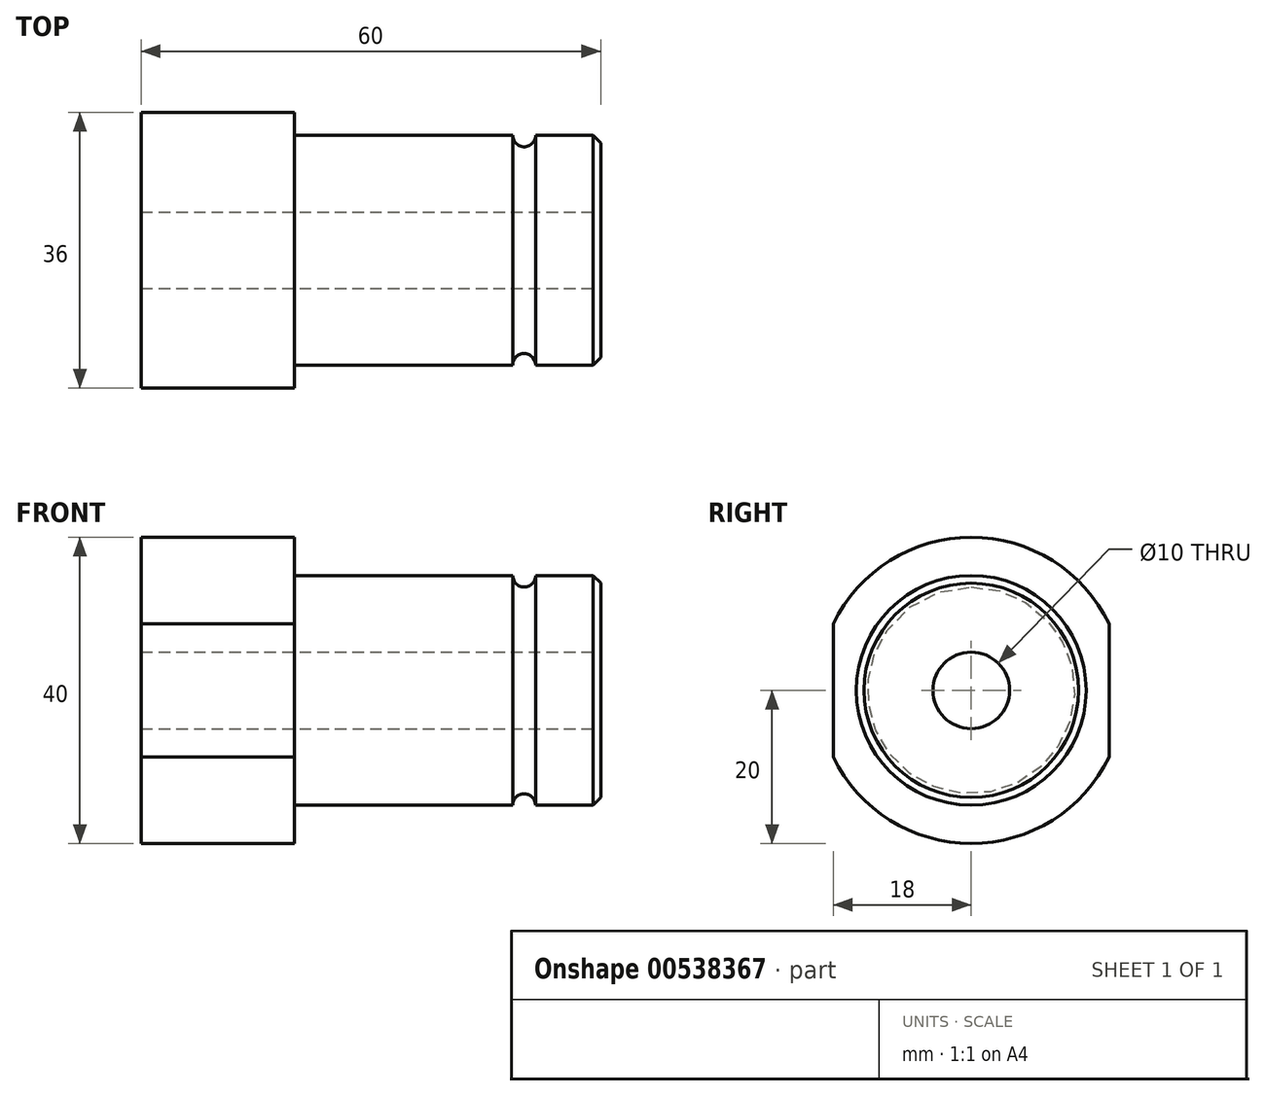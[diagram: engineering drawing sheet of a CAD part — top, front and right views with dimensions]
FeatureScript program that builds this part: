
annotation { "Feature Type Name" : "Feature", "Feature Type Description" : "" }
export const myFeature = defineFeature(function(context is Context, id is Id, definition is map)
    precondition{}
    {
        {
            var Q0;
            Q0=qCreatedBy(makeId("Front.planeOp"),FACE);
            var sketch = newSketch(context, id + "F0", { "sketchPlane" : qUnion([Q0])});
            skLineSegment(sketch, "E0", {"start": v(-37.15, 0) * mm, "end": v(-37.15, 20) * mm});
            skLineSegment(sketch, "E1", {"start": v(-37.15, 20) * mm, "end": v(-17.15, 20) * mm});
            skLineSegment(sketch, "E2", {"start": v(-17.15, 20) * mm, "end": v(-17.15, 15) * mm});
            skLineSegment(sketch, "E3", {"start": v(-17.15, 15) * mm, "end": v(22.85, 15) * mm});
            skLineSegment(sketch, "E4", {"start": v(22.85, 15) * mm, "end": v(22.85, 0) * mm});
            skLineSegment(sketch, "E5", {"start": v(-57.5, 0) * mm, "end": v(58.24, 0) * mm, "construction": true});
            skLineSegment(sketch, "E6", {"start": v(-37.15, 0) * mm, "end": v(22.85, 0) * mm});
            skSolve(sketch);
        }
        {
            var Q0;
            Q0 = qSketchRegion(id + "F0", true);
            var Q1;
            Q1=sQuery(id+"F0.wireOp",EDGE,"E5");
            revolve(context, id + "F1", {"entities" : qUnion([Q0]), "axis" : qUnion([Q1]), "revolveType" : RevolveType.FULL});
        }
        {
            var Q0;
            Q0=qCreatedBy(makeId("Front.planeOp"),FACE);
            var sketch = newSketch(context, id + "F2", { "sketchPlane" : qUnion([Q0])});
            skCircle(sketch, "E7", {"center": v(12.85, 15) * mm, "radius": 1.5 * mm});
            skLineSegment(sketch, "E8", {"start": v(-44.88, 0) * mm, "end": v(52.35, 0) * mm, "construction": true});
            skSolve(sketch);
        }
        {
            var Q0;
            Q0 = qSketchRegion(id + "F2", true);
            var Q1;
            Q1=sQuery(id+"F2.wireOp",EDGE,"E8");
            revolve(context, id + "F3", {"operationType" : NewBodyOperationType.REMOVE, "entities" : qUnion([Q0]), "axis" : qUnion([Q1]), "revolveType" : RevolveType.FULL, "oppositeDirection" : true});
        }
        {
            var Q0;
            Q0=makeQuery(id+"F1.opRevolve","SWEPT_EDGE",EDGE,{"disambiguationData":[OSD([sQuery(id+"F0.wireOp",EDGE,"E3"),sQuery(id+"F0.wireOp",EDGE,"E4")])]});
            chamfer(context, id + "F4", {"entities" : qUnion([Q0]), "width" : 1 * mm, "tangentPropagation" : true});
        }
        {
            var Q0;
            Q0=makeQuery(id+"F1.opRevolve","SWEPT_FACE",FACE,{"disambiguationData":[OSD([sQuery(id+"F0.wireOp",EDGE,"E4")])]});
            var sketch = newSketch(context, id + "F5", { "sketchPlane" : qUnion([Q0])});
            skCircle(sketch, "E9", {"center": v(0, 0) * mm, "radius": 5 * mm});
            skSolve(sketch);
        }
        {
            var Q0;
            Q0 = qSketchRegion(id + "F5", true);
            extrude(context, id + "F6", {"entities" : qUnion([Q0]), "operationType" : NewBodyOperationType.REMOVE, "endBound" : BoundingType.UP_TO_NEXT, "oppositeDirection" : true, "depth" : 25 * mm, "offsetDistance" : 25 * mm});
        }
        {
            var Q0;
            Q0=makeQuery(id+"F1.opRevolve","SWEPT_FACE",FACE,{"disambiguationData":[OSD([sQuery(id+"F0.wireOp",EDGE,"E0")])]});
            var sketch = newSketch(context, id + "F7", { "sketchPlane" : qUnion([Q0])});
            skLineSegment(sketch, "E10.bottom", {"start": v(-18, 20) * mm, "end": v(18, 20) * mm});
            skLineSegment(sketch, "E10.top", {"start": v(-18, -20) * mm, "end": v(18, -20) * mm});
            skLineSegment(sketch, "E10.left", {"start": v(-18, 20) * mm, "end": v(-18, -20) * mm});
            skLineSegment(sketch, "E10.right", {"start": v(18, 20) * mm, "end": v(18, -20) * mm});
            skSolve(sketch);
        }
        {
            var Q0;
            {var subQ0=sQuery(id+"F7.wireOp",EDGE,"E10.right");var subQ1=makeQuery(id+"F1.opRevolve","SWEPT_EDGE",EDGE,{"disambiguationData":[OSD([sQuery(id+"F0.wireOp",EDGE,"E0"),sQuery(id+"F0.wireOp",EDGE,"E1")])]});var subQ2=makeQuery(id+"F7.imprint","INTERSECT",VERTEX,{"disambiguationData":[OD(0.0)],"derivedFrom":[subQ1,subQ0]});Q0=makeQuery(id+"F7.imprint","IMPRINT",FACE,{"disambiguationData":[TD([[makeQuery(id+"F7.imprint","IMPRINT",EDGE,{"disambiguationData":[TD([[subQ2,-1.0]])],"derivedFrom":subQ0}),1.0]])]});}
            var Q1;
            {var subQ0=sQuery(id+"F7.wireOp",EDGE,"E10.left");var subQ1=makeQuery(id+"F1.opRevolve","SWEPT_EDGE",EDGE,{"disambiguationData":[OSD([sQuery(id+"F0.wireOp",EDGE,"E0"),sQuery(id+"F0.wireOp",EDGE,"E1")])]});var subQ2=makeQuery(id+"F7.imprint","INTERSECT",VERTEX,{"disambiguationData":[OD(0.0)],"derivedFrom":[subQ1,subQ0]});Q1=makeQuery(id+"F7.imprint","IMPRINT",FACE,{"disambiguationData":[TD([[makeQuery(id+"F7.imprint","IMPRINT",EDGE,{"disambiguationData":[TD([[subQ2,-1.0]])],"derivedFrom":subQ0}),-1.0]])]});}
            var Q2;
            Q2=makeQuery(id+"F1.opRevolve","SWEPT_FACE",FACE,{"disambiguationData":[OSD([sQuery(id+"F0.wireOp",EDGE,"E2")])]});
            extrude(context, id + "F8", {"entities" : qUnion([Q0, Q1]), "operationType" : NewBodyOperationType.REMOVE, "endBound" : BoundingType.UP_TO_SURFACE, "oppositeDirection" : true, "depth" : 25 * mm, "endBoundEntityFace" : qUnion([Q2]), "offsetDistance" : 25 * mm});
        }
    });
